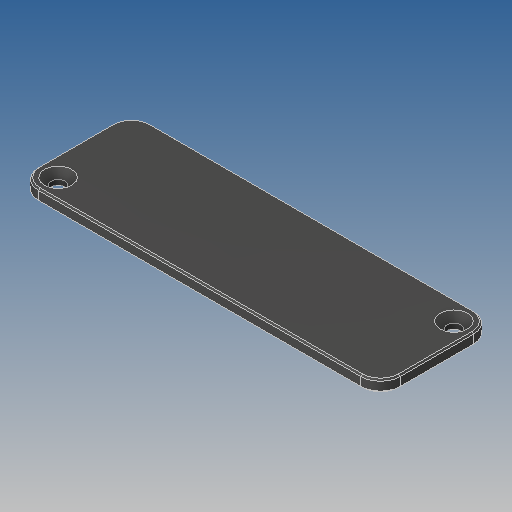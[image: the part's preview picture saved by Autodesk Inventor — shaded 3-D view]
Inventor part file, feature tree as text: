
AUTODESK INVENTOR PART (.ipt)
format: ipt  version: 2019 (Build 230136000, 136)  size: 103,424 bytes
history: native  units: mm
features: chamfer x1
ambient origin geometry x8: Origin, YZ Plane, XZ Plane, XY Plane, X Axis, Y Axis, Z Axis, Center Point
bodies: Solid1 (feature_tree)
feature tree (1):
  chamfer  "Chamfer1"  [1 undecoded]
note: 1 required parameter value undecoded (feature->parameter linkage not recoverable at this tier; creation-order binding heuristic only, values carry confidence <= 0.55)
